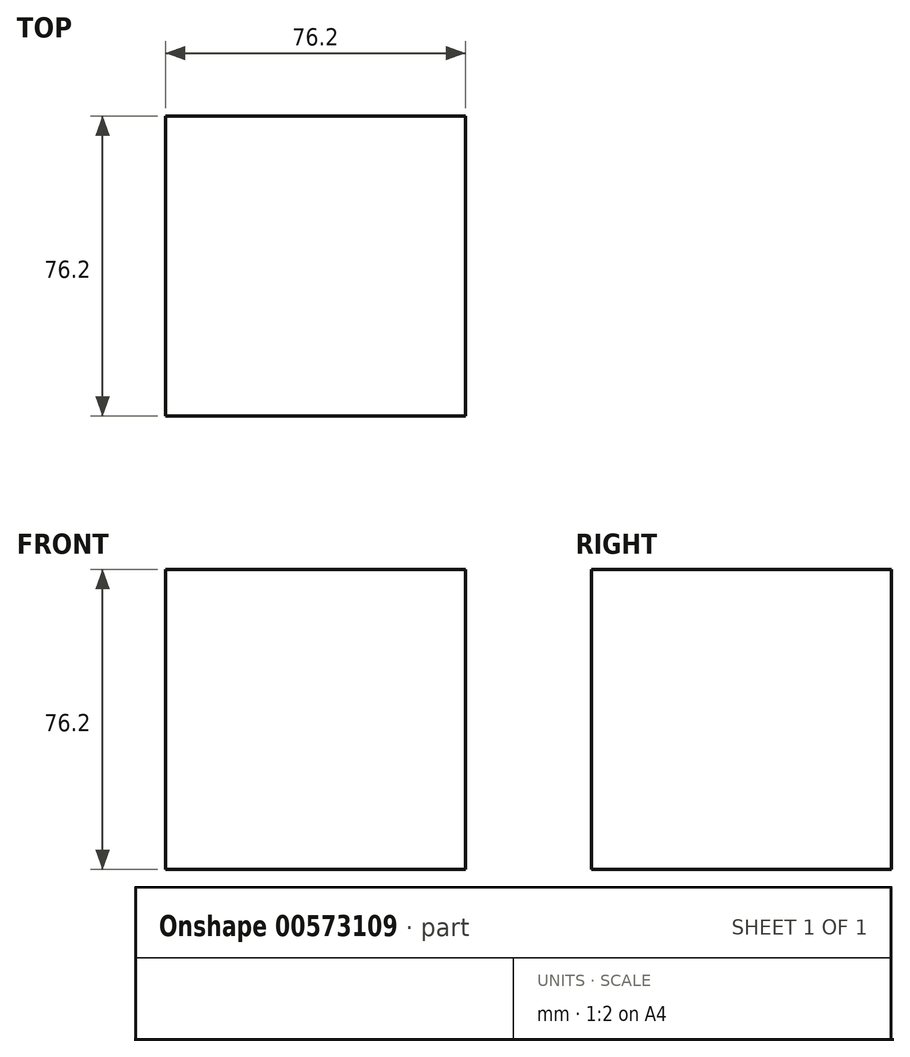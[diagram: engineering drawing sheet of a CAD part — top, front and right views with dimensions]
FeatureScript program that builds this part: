
annotation { "Feature Type Name" : "Feature", "Feature Type Description" : "" }
export const myFeature = defineFeature(function(context is Context, id is Id, definition is map)
    precondition{}
    {
        {
            var Q0;
            Q0=qCreatedBy(makeId("Front.planeOp"),FACE);
            var sketch = newSketch(context, id + "F0", { "sketchPlane" : qUnion([Q0])});
            skLineSegment(sketch, "E0.bottom", {"start": v(-37.34, -34.21) * mm, "end": v(38.86, -34.21) * mm});
            skLineSegment(sketch, "E0.top", {"start": v(-37.34, 41.99) * mm, "end": v(38.86, 41.99) * mm});
            skLineSegment(sketch, "E0.left", {"start": v(-37.34, -34.21) * mm, "end": v(-37.34, 41.99) * mm});
            skLineSegment(sketch, "E0.right", {"start": v(38.86, -34.21) * mm, "end": v(38.86, 41.99) * mm});
            skSolve(sketch);
        }
        {
            var Q0;
            Q0=makeQuery(id+"F0.imprint","IMPRINT",FACE,{"disambiguationData":[TD([[makeQuery(id+"F0.imprint","IMPRINT",EDGE,{"derivedFrom":sQuery(id+"F0.wireOp",EDGE,"E0.bottom")}),1.0]])]});
            extrude(context, id + "F1", {"entities" : qUnion([Q0]), "depth" : 76.2 * mm, "offsetDistance" : 25.4 * mm});
        }
    });
